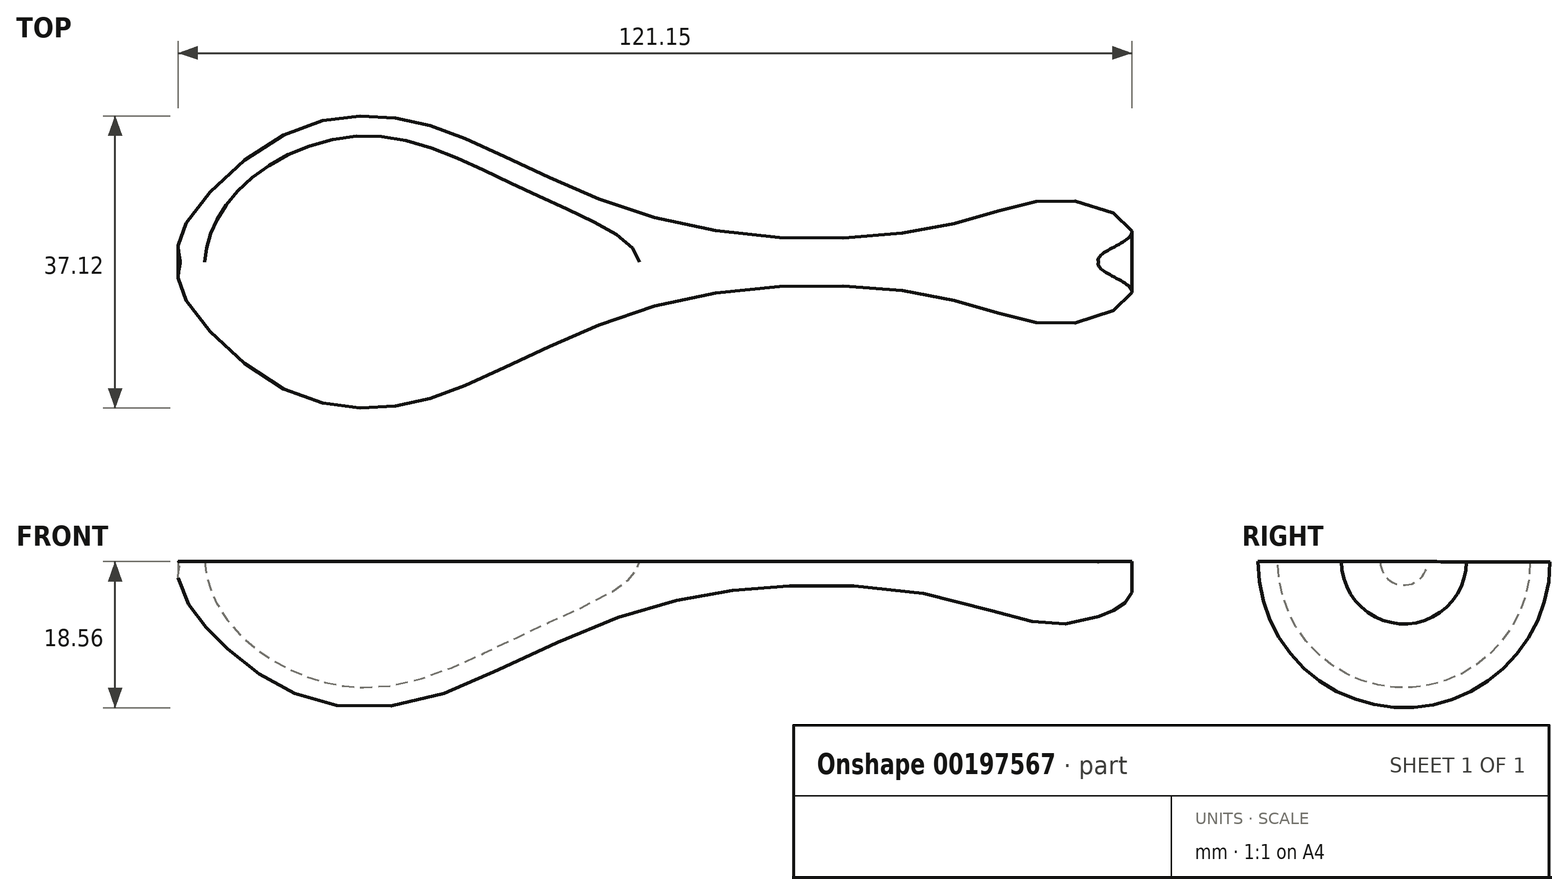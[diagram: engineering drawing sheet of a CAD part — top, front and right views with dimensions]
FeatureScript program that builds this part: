
annotation { "Feature Type Name" : "Feature", "Feature Type Description" : "" }
export const myFeature = defineFeature(function(context is Context, id is Id, definition is map)
    precondition{}
    {
        {
            var Q0;
            Q0=qCreatedBy(makeId("Top.planeOp"),FACE);
            var sketch = newSketch(context, id + "F0", { "sketchPlane" : qUnion([Q0])});
            skLineSegment(sketch, "E0", {"start": v(61.04, 0) * mm, "end": v(2.7, 0) * mm});
            skFitSpline(sketch, "E1", {"points": [v(-55.63, 0) * mm, v(-55.63, -3.46) * mm, v(-44.12, -15.23) * mm, v(-30.06, -18.49) * mm, v(-17.78, -14.98) * mm, v(6.98, -5.02) * mm, v(41.86, -4.66) * mm, v(57.77, -7.8) * mm, v(65.15, -3.45) * mm, v(61.04, 0) * mm], "startDerivative": vector(-8.42, -68.1) * mm, "endDerivative": vector(25.17, 53.4) * mm});
            skFitSpline(sketch, "E2", {"points": [v(-52.56, 0) * mm, v(-50.83, -5.64) * mm, v(-44.12, -12.4) * mm, v(-30.06, -15.94) * mm, v(-10.44, -8.5) * mm, v(2.7, 0) * mm], "startDerivative": vector(5.05, -41.25) * mm, "endDerivative": vector(4.51, 41.87) * mm});
            skLineSegment(sketch, "E3.trimOffspring", {"start": v(-52.56, 0) * mm, "end": v(-55.63, 0) * mm});
            skSolve(sketch);
        }
        {
            var Q0;
            Q0=makeQuery(id+"F0.imprint","IMPRINT",FACE,{"disambiguationData":[TD([[makeQuery(id+"F0.imprint","IMPRINT",EDGE,{"derivedFrom":sQuery(id+"F0.wireOp",EDGE,"E0")}),1.0]])]});
            var Q1;
            Q1=sQuery(id+"F0.wireOp",EDGE,"E3.trimOffspring");
            revolve(context, id + "F1", {"entities" : qUnion([Q0]), "axis" : qUnion([Q1]), "revolveType" : RevolveType.ONE_DIRECTION, "oppositeDirection" : true, "angle" : 179.77 * degree});
        }
    });
